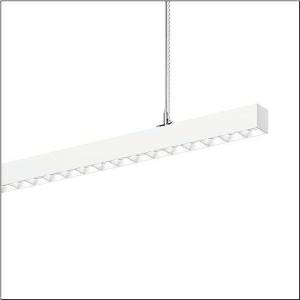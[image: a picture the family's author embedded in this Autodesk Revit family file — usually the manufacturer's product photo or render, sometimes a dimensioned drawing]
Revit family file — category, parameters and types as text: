
# Revit family: silica_r__21_51mx36da47wb_ab97
name_source: partatom
category: Lighting Fixtures
units: mm (PartAtom-declared; Revit-internal decimal feet)

## family parameters
Cut with Voids When Loaded = No
Host = Face
Light Source = No
Part Type = Normal
Room Calculation Point = No
Round Connector Dimension = Use Diameter
Shared = No

## types (1)
- --- (1 x LED, 7060 lm, 40.3 W, 4000K)
    Apparent Load = 40 VA
    CIE Flux Codes = 83 98 100 61 100
    Color Rendering = 80
    Color Temperature = 4000K
    Default Elevation = 1800 mm
    Description = Silica® 21, office luminaire, primary light control with darklight reflector, of PMMA, white, CAT 2 (L<= 3000cd/m²), light emission: direct/indirect distribution, primary light characteristic: symmetric, installation type: suspended mounting, LED, rated luminous flux: 7.060lm, luminous efficacy: 175lm/W, light colour: 840, colour temperature: 4000K, with terminal, 3+2-pole, max. 2.5mm², mains connection: 220..240V, AC, 50/60Hz, rated input power: 40.3W, luminaire housing, of aluminium, traffic white (RAL 9016), length: 1.204mm, width: 53mm, height: 53mm, protection rating (complete): IP20, insulation class (complete): insulation class I (protective earthing), certification: CE, permissible operating ambient temperature: 0..+35°C, standard: EN 50419, packaging unit: 1 piece
    Height = 53 mm
    Lamp = 1 x LED
    Lamp Light Flux = 7060 lm
    Lamp Power = 40.3 W
    Lamp count = 1
    Length = 1204 mm
    Luminous efficacy = 175 lm/W
    Manufacturer = Siteco
    ModVariant = No
    Model = 51MX36DA47WB
    Mounting Place = Ceiling
    Mounting Type = Pendant
    Number of Poles = 1
    OnlyDefault = Yes
    Power Factor = 1
    Product Name = Silica® 21
    Product group = office luminaire | ceiling pendant
    ProductGroupID = 905
    Protection Class = Protection class I
    Protection Degree = IP 20
    RLX_Detail_Level = 1
    RlxData = <blob elided: 40785 chars, md5=8f0e955a>
    Socket = socket
    Standby Power = 0 W
    System Light Flux = 7060 lm
    System Power = 40 W
    Type Comments = factory setting: luminous flux: 100 % | dim-lin: 254 | 336 mA
    Type Image = l_1251641.jpg
    URL = http://relux.com
    VarID = @adj_030455
    Voltage = 0 V
    Weight = 0.00 kg
    Width = 53 mm

## geometry (parser evidence)
native form markers: Blend x4, Sweep x13
no freeform markers — native parametric forms only
